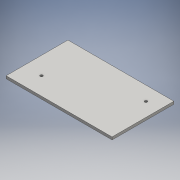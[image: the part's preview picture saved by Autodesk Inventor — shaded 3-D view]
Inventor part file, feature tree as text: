
AUTODESK INVENTOR PART (.ipt)
format: ipt  version: 2016 (Build 200138000, 138)  size: 93,696 bytes
history: native  units: mm
features: other x1, extrude x1, sketch x1
ambient origin geometry x8: Origin, YZ Plane, XZ Plane, XY Plane, X Axis, Y Axis, Z Axis, Center Point
bodies: Body1 (feature_tree)
feature tree (3):
  other  "ソリッド1"
  extrude  "押し出し1"  Depth=3.0mm
  sketch  "スケッチ1"
